# Revit family: Fireplace_Gas_Heatilator_Heirloom
name_source: partatom
category: Mechanical Equipment
revit_build: Autodesk Revit 2015 (Build: 20140323_1530(x64)
units: mm (PartAtom-declared; Revit-internal decimal feet)

## types (6) — shared parameters
Assembly Code = D3020
Construction Details = http://www.arcat.com
Default Elevation = 0' - 0"
Electrical_Voltage = 120 V
Fixture Finish = Metal - Heatilator - Metallic Black
Fuel Consumption = as Specified
HVAC_BTU Output = 0.0 Btu/h
Heating Capacity = as Specified
Keynote = 10305
Manufacturer = Heatilator
Manufacturer Website = http://www.heatilator.com
Product Data = http://www.arcat.com
Revision = R2_2014-09
Sales Information = http://www.heatilator.com
Send Message = http://www.arcat.com
Specification = http://www.arcat.com
Standards Conformance = UL  ;  cUL
URL = http://www.heatilator.com
Unit Depth = 2' - 0"
zero-valued in all types: Expected Lifespan (Years), Maintenance Schedule (Months), Unit Weight, Warranty Duration (Years)

## per-type parameters (varying)
| type | Description | Efficiency Ratings | Fuel Type | HVAC_BTU Input | Model | Opening Height | Opening Width | Unit Height | Unit Width |
| 50x40 Viewing Area LP | Heatilator Gas Burning Fireplace - Heirloom HEIR50 LP as Specified | Steady State 68.2  ;  AFUE 66  ;  EnerGuide 67.5 | LP | 63500.0 Btu/h | HEIR50 | 3' - 4 1/16" | 4' - 1 7/8" | 5' - 6 5/8" | 6' - 3" |
| 50x40 Viewing Area NG | Heatilator Gas Burning Fireplace - Heirloom HEIR50 NG as Specified | Steady State 68.2  ;  AFUE 66  ;  EnerGuide 67.5 | NG | 65000.0 Btu/h | HEIR50 | 3' - 4 1/16" | 4' - 1 7/8" | 5' - 6 5/8" | 6' - 3" |
| 42x36 Viewing Area LP | Heatilator Gas Burning Fireplace - Heirloom HEIR42 LP as Specified | Steady State 77.2  ;  AFUE 66.7  ;  EnerGuide 67 | LP | 51000.0 Btu/h | HEIR42 | 3' - 0 1/16" | 3' - 5 7/8" | 5' - 2 5/8" | 5' - 7" |
| 42x36 Viewing Area NG | Heatilator Gas Burning Fireplace - Heirloom HEIR42 NG as Specified | Steady State 77.2  ;  AFUE 66.7  ;  EnerGuide 67 | NG | 54000.0 Btu/h | HEIR42 | 3' - 0 1/16" | 3' - 5 7/8" | 5' - 2 5/8" | 5' - 7" |
| 36x31 Viewing Area LP | Heatilator Gas Burning Fireplace - Heirloom HEIR36 LP as Specified | Steady State 76.2  ;  AFUE 56.7  ;  EnerGuide 59.6 | LP | 44000.0 Btu/h | HEIR36 | 2' - 7 1/16" | 2' - 11 7/8" | 4' - 9 5/8" | 5' - 1" |
| 36x31 Viewing Area NG | Heatilator Gas Burning Fireplace - Heirloom HEIR36 NG as Specified | Steady State 76.2  ;  AFUE 56.7  ;  EnerGuide 59.6 | NG | 45500.0 Btu/h | HEIR36 | 2' - 7 1/16" | 2' - 11 7/8" | 4' - 9 5/8" | 5' - 1" |

## geometry (parser evidence)
native form markers: Blend x4, Sweep x6
no freeform markers — native parametric forms only
